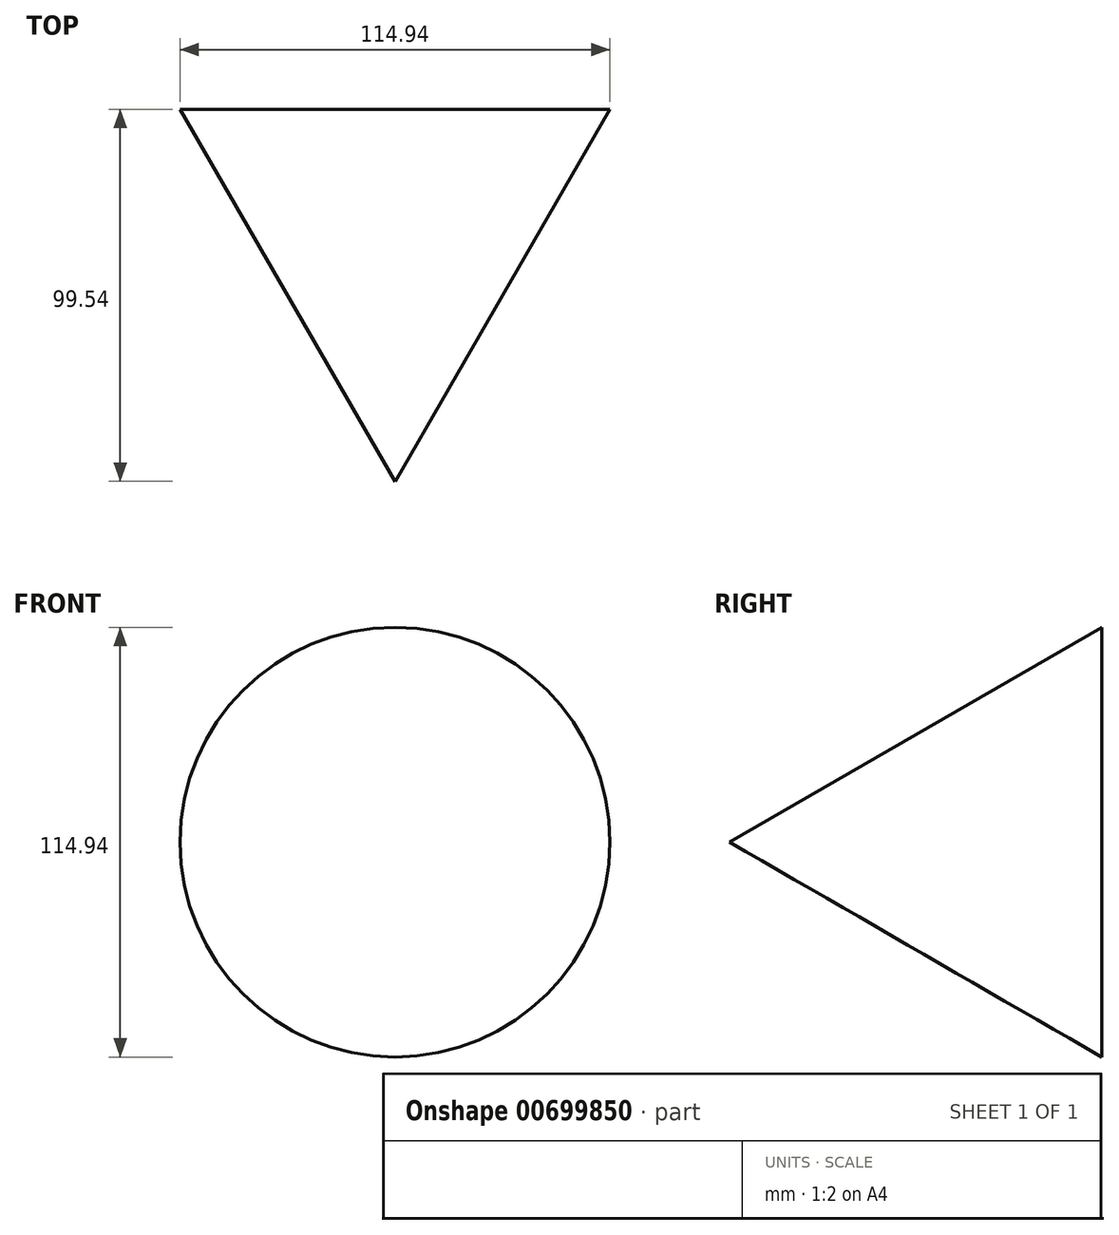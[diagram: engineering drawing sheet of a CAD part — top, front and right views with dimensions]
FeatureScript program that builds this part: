
annotation { "Feature Type Name" : "Feature", "Feature Type Description" : "" }
export const myFeature = defineFeature(function(context is Context, id is Id, definition is map)
    precondition{}
    {
        {
            var Q0;
            Q0=qCreatedBy(makeId("Front.planeOp"),FACE);
            var sketch = newSketch(context, id + "F0", { "sketchPlane" : qUnion([Q0])});
            skCircle(sketch, "E0", {"center": v(0, -2.13) * mm, "radius": 57.47 * mm});
            skSolve(sketch);
        }
        {
            var Q0;
            Q0=makeQuery(id+"F0.imprint","IMPRINT",FACE,{"disambiguationData":[TD([[makeQuery(id+"F0.imprint","IMPRINT",EDGE,{"derivedFrom":sQuery(id+"F0.wireOp",EDGE,"E0")}),1.0]])]});
            extrude(context, id + "F1", {"entities" : qUnion([Q0]), "depth" : 101.6 * mm, "offsetDistance" : 25.4 * mm, "hasDraft" : true, "draftAngle" : 30 * degree, "draftPullDirection" : true});
        }
    });
